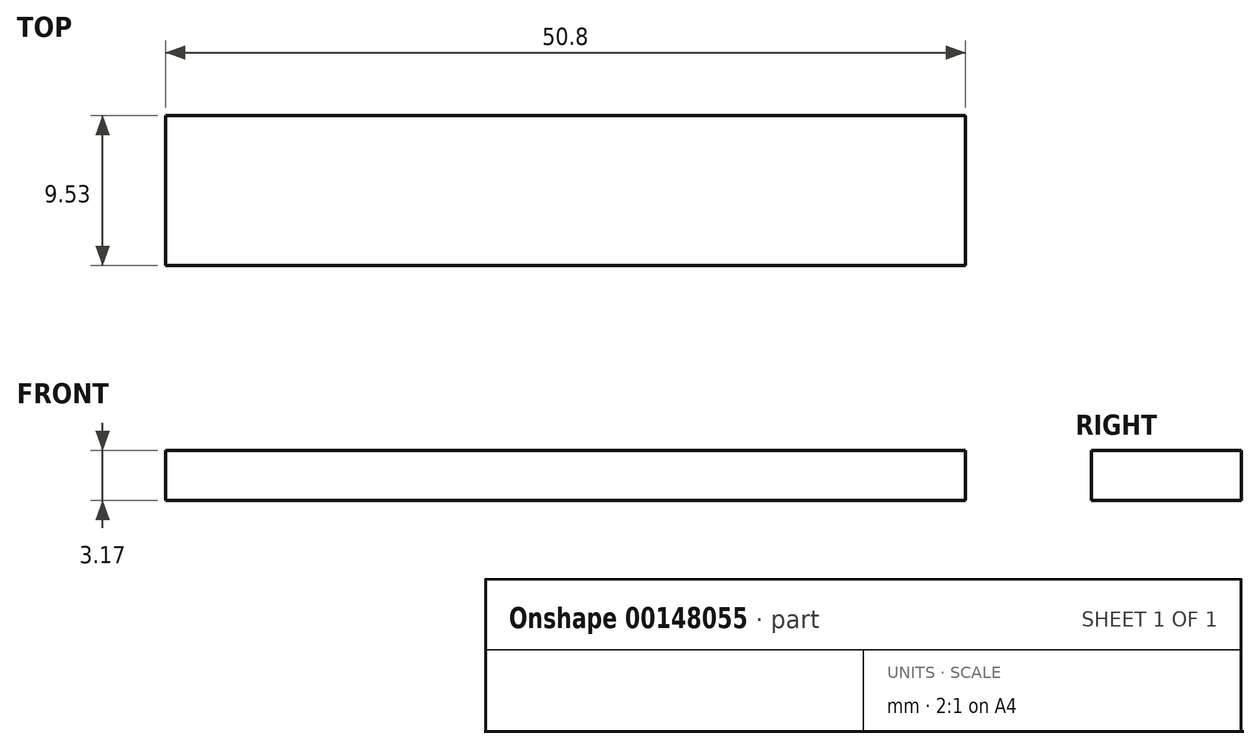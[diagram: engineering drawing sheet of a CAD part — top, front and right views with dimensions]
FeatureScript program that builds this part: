
annotation { "Feature Type Name" : "Feature", "Feature Type Description" : "" }
export const myFeature = defineFeature(function(context is Context, id is Id, definition is map)
    precondition{}
    {
        {
            var Q0;
            Q0=qCreatedBy(makeId("Top.planeOp"),FACE);
            var sketch = newSketch(context, id + "F0", { "sketchPlane" : qUnion([Q0])});
            skLineSegment(sketch, "E0.bottom", {"start": v(0, 0) * mm, "end": v(50.8, 0) * mm});
            skLineSegment(sketch, "E0.top", {"start": v(0, -9.53) * mm, "end": v(50.8, -9.53) * mm});
            skLineSegment(sketch, "E0.left", {"start": v(0, 0) * mm, "end": v(0, -9.53) * mm});
            skLineSegment(sketch, "E0.right", {"start": v(50.8, 0) * mm, "end": v(50.8, -9.53) * mm});
            skSolve(sketch);
        }
        {
            var Q0;
            Q0=qSketchRegion(id+"F0",true);
            extrude(context, id + "F1", {"entities" : qUnion([Q0]), "depth" : 3.17 * mm});
        }
    });
